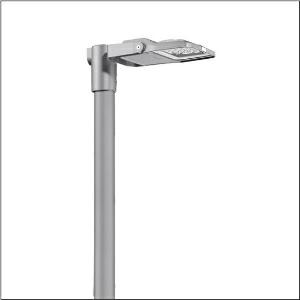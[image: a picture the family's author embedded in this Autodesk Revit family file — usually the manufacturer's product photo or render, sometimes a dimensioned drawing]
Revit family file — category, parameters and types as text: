
# Revit family: floodlight_fl_21_iq_micro___pl33t_5xa7762a4f3a_b73c
name_source: partatom
category: Lighting Fixtures
units: mm (PartAtom-declared; Revit-internal decimal feet)

## family parameters
Cut with Voids When Loaded = No
Host = Face
Light Source = No
Part Type = Normal
Room Calculation Point = No
Round Connector Dimension = Use Diameter
Shared = No

## types (1)
- --- (1 x LED, 3050 lm, 23.1 W, 4000K)
    Apparent Load = 23 VA
    CIE Flux Codes = 26 75 99 100 100
    Color Rendering = 70
    Color Temperature = 4000K
    Default Elevation = 1800 mm
    Description = Floodlight FL 21 iQ micro, floodlight, primary light control with lens, of PMMA, primary optical cover: protective disc, of toughened safety glass, transparent, light distribution: PL33T, light emission: direct distribution, installation type: surface-mounted, LED, High Power LED, rated luminous flux: 3.050lm, luminous efficacy: 132lm/W, light colour: 740, colour temperature: 4000K, control: Auto-Match, Temp-Guard, Night-Set, Smart-Wire, Desk-Remote (wireless, voltage-free reading and setting of iQ features in the workshop via application-optimized NFC function/RFID function), optimised constant luminous flux control (CLO 2.0), Street-Remote, with terminal, 6-pole, mains connection: 220..240V, AC, 50/60Hz, start of lifetime: 23W, end of service life: 24W, reduction: 11W, luminaire housing, of diecast aluminium, powder-coated, Siteco® metallic grey (DB 702S), corrosivity category C5 mid according to DIN EN ISO 12944, sealing non-destructively replaceable, please order mast flange separately, mast bracket, of steel, galvanised, powder-coated, Siteco® metallic grey (DB 702S), protection rating (complete): IP66, insulation class (complete): insulation class II (safety insulation), certification: CE, ENEC, VDE, protection symbol: D, impact resistance: IK07, permissible operating ambient temperature: -40..+40°C, permissible operating ambient temperature for outdoor applications: -40..+50°C, standard: DIN EN 12944, LABS conformity tested according to VDMA 24364:2018-05, packaging unit: 1 piece

Light Distribution: PL33T
    Height = 65 mm
    Lamp = 1 x LED
    Lamp Light Flux = 3050 lm
    Lamp Power = 23.1 W
    Lamp count = 1
    Length = 312 mm
    Luminous efficacy = 132 lm/W
    Manufacturer = Siteco
    ModVariant = No
    Model = 5XA7762A4F3A
    Number of Poles = 1
    OnlyDefault = Yes
    Power Factor = 1
    Product Name = Floodlight FL 21 iQ micro | PL33T
    Product group = floodlight | pylon annexe
    ProductGroupID = 6200
    Protection Class = Protection class II
    Protection Degree = IP 66
    RLX_Detail_Level = 1
    RLX_Emergency_Light_Flux = 0 lm
    RLX_Emergency_Type = 0
    RLX_Emergency_Type_DB = No
    RlxData = <blob elided: 101577 chars, md5=d9e17fca>
    Socket = socket
    Standby Power = 0 W
    System Light Flux = 3050 lm
    System Power = 23 W
    Type Comments = factory setting: luminous flux: 100 % | dim-lin: 254 | 455 mA
    Type Image = l_1007121.jpg
    URL = http://relux.com
    VarID = @adj_118199
    Voltage = 0 V
    Weight = 0.00 kg
    Width = 230 mm

## geometry (parser evidence)
native form markers: Blend x4, Sweep x10
no freeform markers — native parametric forms only
